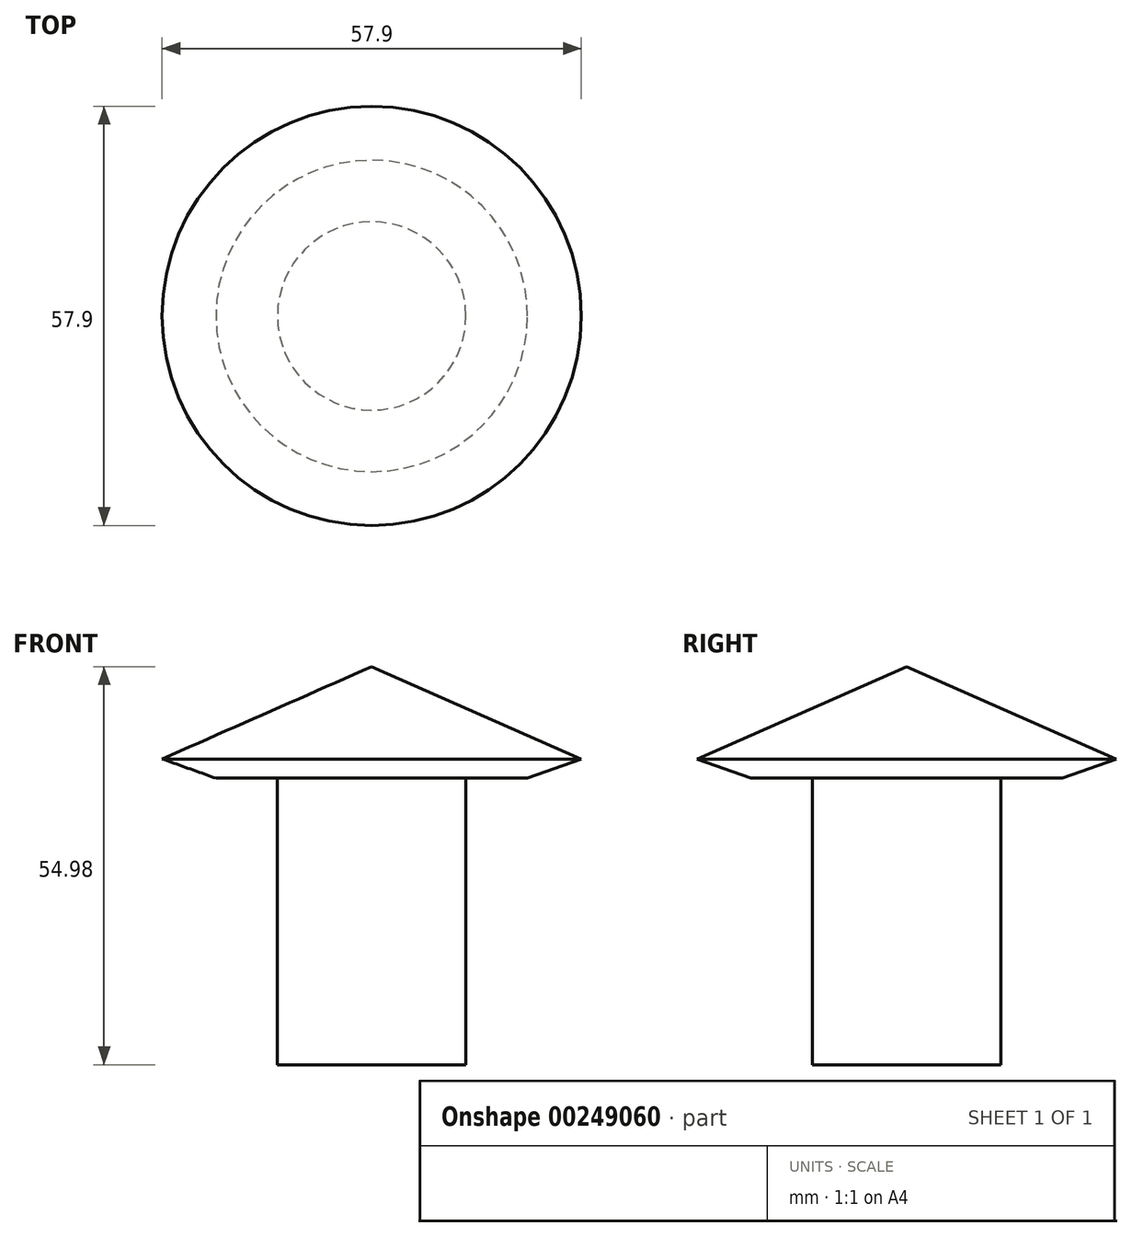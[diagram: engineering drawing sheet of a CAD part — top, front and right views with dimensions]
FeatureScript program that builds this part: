
annotation { "Feature Type Name" : "Feature", "Feature Type Description" : "" }
export const myFeature = defineFeature(function(context is Context, id is Id, definition is map)
    precondition{}
    {
        {
            var Q0;
            Q0=qCreatedBy(makeId("Front.planeOp"),FACE);
            var sketch = newSketch(context, id + "F0", { "sketchPlane" : qUnion([Q0])});
            skLineSegment(sketch, "E0", {"start": v(0, 48.47) * mm, "end": v(-28.95, 35.72) * mm});
            skLineSegment(sketch, "E1", {"start": v(-28.95, 35.72) * mm, "end": v(-21.51, 33.07) * mm});
            skLineSegment(sketch, "E2", {"start": v(-21.51, 33.07) * mm, "end": v(-13.01, 33.07) * mm});
            skLineSegment(sketch, "E3", {"start": v(-13.01, 33.07) * mm, "end": v(-13.01, -6.5) * mm});
            skLineSegment(sketch, "E4", {"start": v(-13.01, -6.5) * mm, "end": v(0, -6.5) * mm});
            skLineSegment(sketch, "E5", {"start": v(0, -6.5) * mm, "end": v(0, 48.47) * mm});
            skSolve(sketch);
        }
        {
            var Q0;
            Q0=makeQuery(id+"F0.imprint","IMPRINT",FACE,{"disambiguationData":[TD([[makeQuery(id+"F0.imprint","IMPRINT",EDGE,{"derivedFrom":sQuery(id+"F0.wireOp",EDGE,"E0")}),1.0]])]});
            var Q1;
            Q1=sQuery(id+"F0.wireOp",EDGE,"E5");
            revolve(context, id + "F1", {"entities" : qUnion([Q0]), "axis" : qUnion([Q1]), "revolveType" : RevolveType.FULL});
        }
    });
